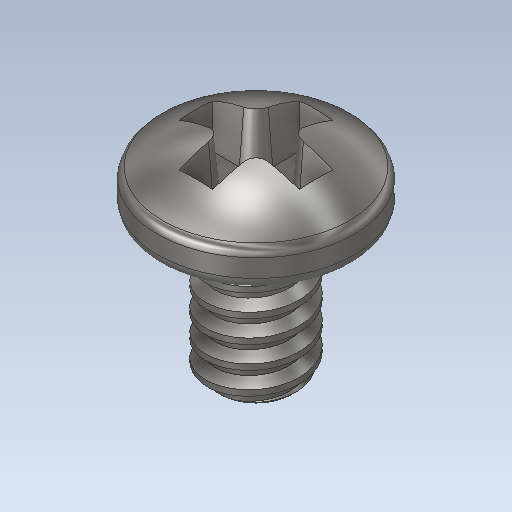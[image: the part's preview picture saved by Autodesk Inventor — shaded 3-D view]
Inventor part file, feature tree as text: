
AUTODESK INVENTOR PART (.ipt)
format: ipt  version: 2020 (Build 240168000, 168)  size: 451,584 bytes
history: native  units: in
note: dims shown in document units (in); Inventor stores cm internally (conversion verified against a paired STEP export)
features: other x60, sketch x4, extrude x2, revolve x1, helix x1, plane x1
ambient origin geometry x8: Origin, YZ Plane, XZ Plane, XY Plane, X Axis, Y Axis, Z Axis, Center Point
bodies: Solid1 (feature_tree)
feature tree (69):
  other  "Table"
  other  "Length = 0.1875"
  other  "Length = 0.375"
  other  "Length = 0.3125"
  other  "Length = 0.5"
  other  "Length = 2.5"
  other  "Length = 0.6875"
  other  "Length = 0.75"
  other  "Length = 0.875"
  other  "Length = 1"
  other  "Length = 1.25"
  other  "Length = 1.5"
  other  "TPI = 56"
  other  "Gauge = 2"
  other  "Length = 0.15625"
  other  "Length = 0.125"
  other  "Length = 0.21875"
  other  "Length = 0.25"
  other  "Length = 0.4375"
  other  "Length = 0.5625"
  other  "Length = 1.125"
  other  "Length = 1.75"
  other  "Length = 2"
  other  "Length = 2.75"
  other  "TPI = 40"
  other  "Gauge = 4"
  other  "Length = 3"
  other  "Length = 2.25"
  other  "Length = 1.375"
  other  "Length = 1.625"
  other  "Length = 1.875"
  other  "Gauge = 8"
  other  "TPI = 32"
  other  "Length = 4"
  other  "Length = 6"
  other  "Gauge = 10"
  other  "Length = 3.5"
  other  "Gauge = 12"
  other  "TPI = 24"
  other  "Length = 4.5"
  other  "Gauge = 6"
  other  "Length = 5"
  other  "Gauge = 1/4"
  other  "TPI = 20"
  other  "TPI = 48"
  other  "TPI = 28"
  other  "Gauge = 0"
  other  "TPI = 80"
  other  "Length = 0.09375"
  other  "Length = 0.28125"
  other  "Length = 0.34375"
  other  "TPI = 64"
  other  "Gauge = 1"
  other  "TPI = 72"
  other  "Gauge = 3"
  other  "Gauge = 5"
  other  "Gauge = 5/16"
  other  "TPI = 18"
  other  "Gauge = 3/8"
  other  "TPI = 16"
  revolve  "Revolution1"  Angle=45.0deg
  helix  "Coil1"  [1 undecoded]
  extrude  "Extrusion1"  Depth=0.219in
  plane  "Work Plane1"
  extrude  "Extrusion3"  TaperAngle=90.0deg  [1 undecoded]
  sketch  "Sketch1"  dims[d0=0.08in d2=45.0deg d3=0.0125in]
  sketch  "Sketch2"  dims[d4=0.1047in d5=0.219in]
  sketch  "Sketch3"  dims[d6=0.02in d7=90.0deg]
  sketch  "Sketch6"  dims[d8=0.17in d9=0.1562in d11=0.3125in d12=60.0deg d13=0.0188in d14=0.0063in d15=0.025in d16=0.1938in d17=0.3937in d18=0.0in d19=90.0deg d20=90.0deg d21=0.0in d22=0.0in d23=1.0in d24=0.0in d40=0.1369in d41=0.04in d42=0.0133in d43=0.06in d44=-0.0344in d45=40.0in d46=4.0in]
note: 2 required parameter values undecoded (feature->parameter linkage not recoverable at this tier; creation-order binding heuristic only, values carry confidence <= 0.55)
